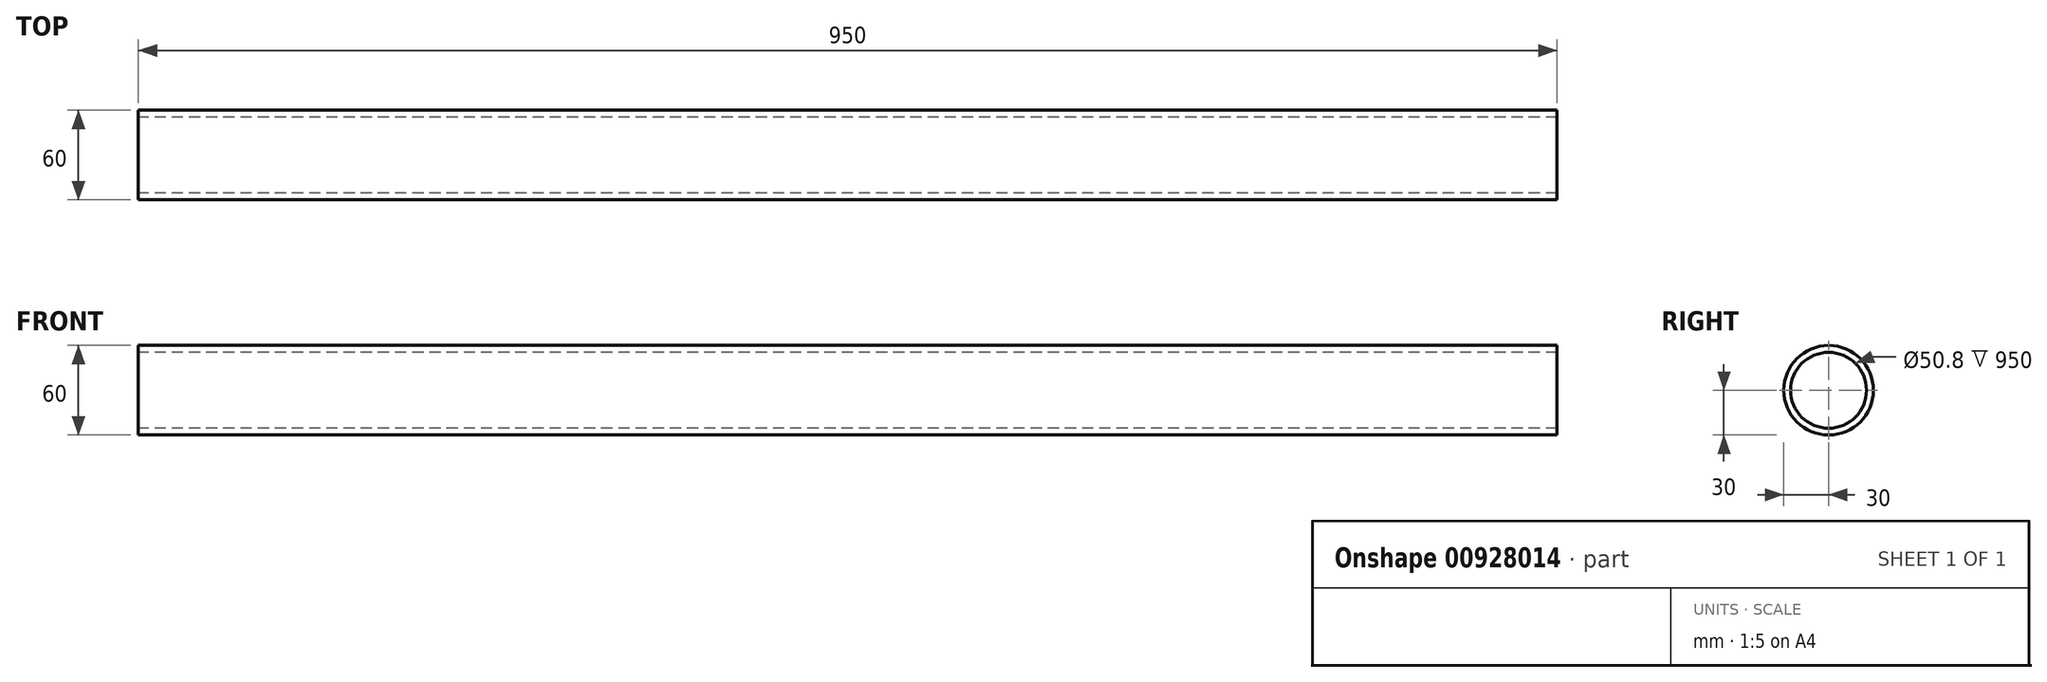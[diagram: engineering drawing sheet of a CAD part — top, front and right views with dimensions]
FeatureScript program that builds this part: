
annotation { "Feature Type Name" : "Feature", "Feature Type Description" : "" }
export const myFeature = defineFeature(function(context is Context, id is Id, definition is map)
    precondition{}
    {
        {
            var Q0;
            Q0=qCreatedBy(makeId("Right.planeOp"),FACE);
            var sketch = newSketch(context, id + "F0", { "sketchPlane" : qUnion([Q0])});
            skCircle(sketch, "E0", {"center": v(0, 0) * mm, "radius": 30 * mm});
            skCircle(sketch, "E1", {"center": v(0, 0) * mm, "radius": 25.4 * mm});
            skSolve(sketch);
        }
        {
            var Q0;
            Q0 = qSketchRegion(id + "F0", true);
            extrude(context, id + "F1", {"entities" : qUnion([Q0]), "depth" : 950 * mm, "offsetDistance" : 25 * mm});
        }
    });
